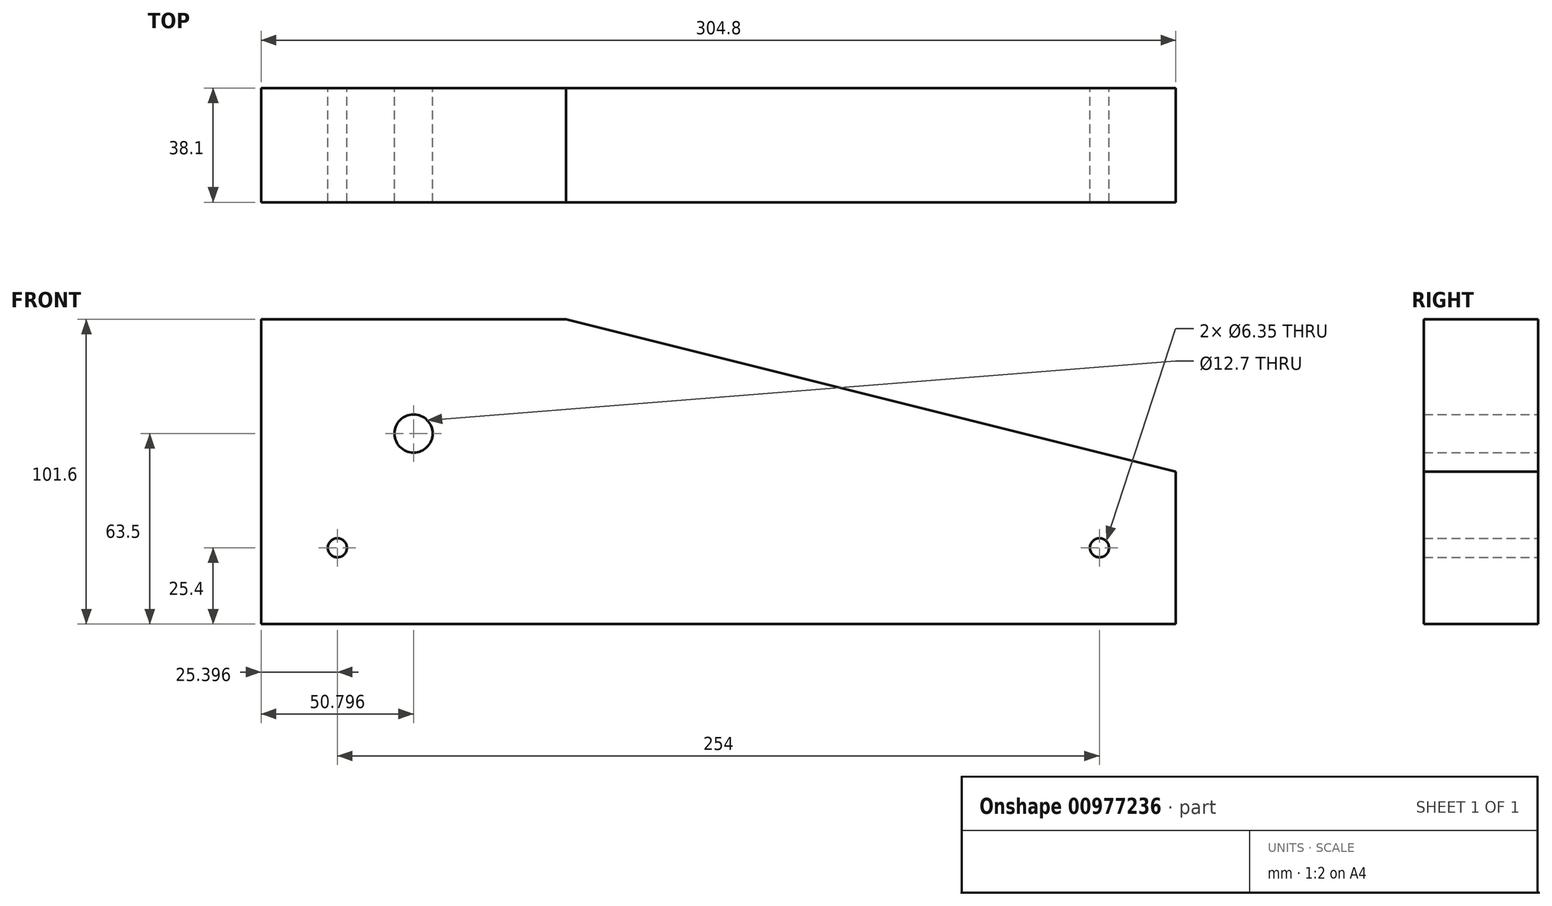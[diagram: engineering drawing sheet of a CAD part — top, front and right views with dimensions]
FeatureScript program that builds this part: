
annotation { "Feature Type Name" : "Feature", "Feature Type Description" : "" }
export const myFeature = defineFeature(function(context is Context, id is Id, definition is map)
    precondition{}
    {
        {
            var Q0;
            Q0=qCreatedBy(makeId("Front.planeOp"),FACE);
            var sketch = newSketch(context, id + "F0", { "sketchPlane" : qUnion([Q0])});
            skLineSegment(sketch, "E0", {"start": v(-159.18, 101.6) * mm, "end": v(-159.18, 0) * mm});
            skLineSegment(sketch, "E1", {"start": v(-159.18, 0) * mm, "end": v(145.62, 0) * mm});
            skLineSegment(sketch, "E2", {"start": v(145.62, 0) * mm, "end": v(145.62, 50.8) * mm});
            skLineSegment(sketch, "E3", {"start": v(145.62, 50.8) * mm, "end": v(-57.58, 101.6) * mm});
            skLineSegment(sketch, "E4", {"start": v(-57.58, 101.6) * mm, "end": v(-159.18, 101.6) * mm});
            skCircle(sketch, "E5", {"center": v(-108.38, 63.5) * mm, "radius": 6.35 * mm});
            skCircle(sketch, "E6", {"center": v(-133.78, 25.4) * mm, "radius": 3.18 * mm});
            skCircle(sketch, "E7", {"center": v(120.22, 25.4) * mm, "radius": 3.18 * mm});
            skSolve(sketch);
        }
        {
            var Q0;
            Q0=makeQuery(id+"F0.imprint","IMPRINT",FACE,{"disambiguationData":[TD([[makeQuery(id+"F0.imprint","IMPRINT",EDGE,{"derivedFrom":sQuery(id+"F0.wireOp",EDGE,"E0")}),1.0]])]});
            extrude(context, id + "F1", {"entities" : qUnion([Q0]), "depth" : 38.1 * mm, "offsetDistance" : 25.4 * mm});
        }
    });
